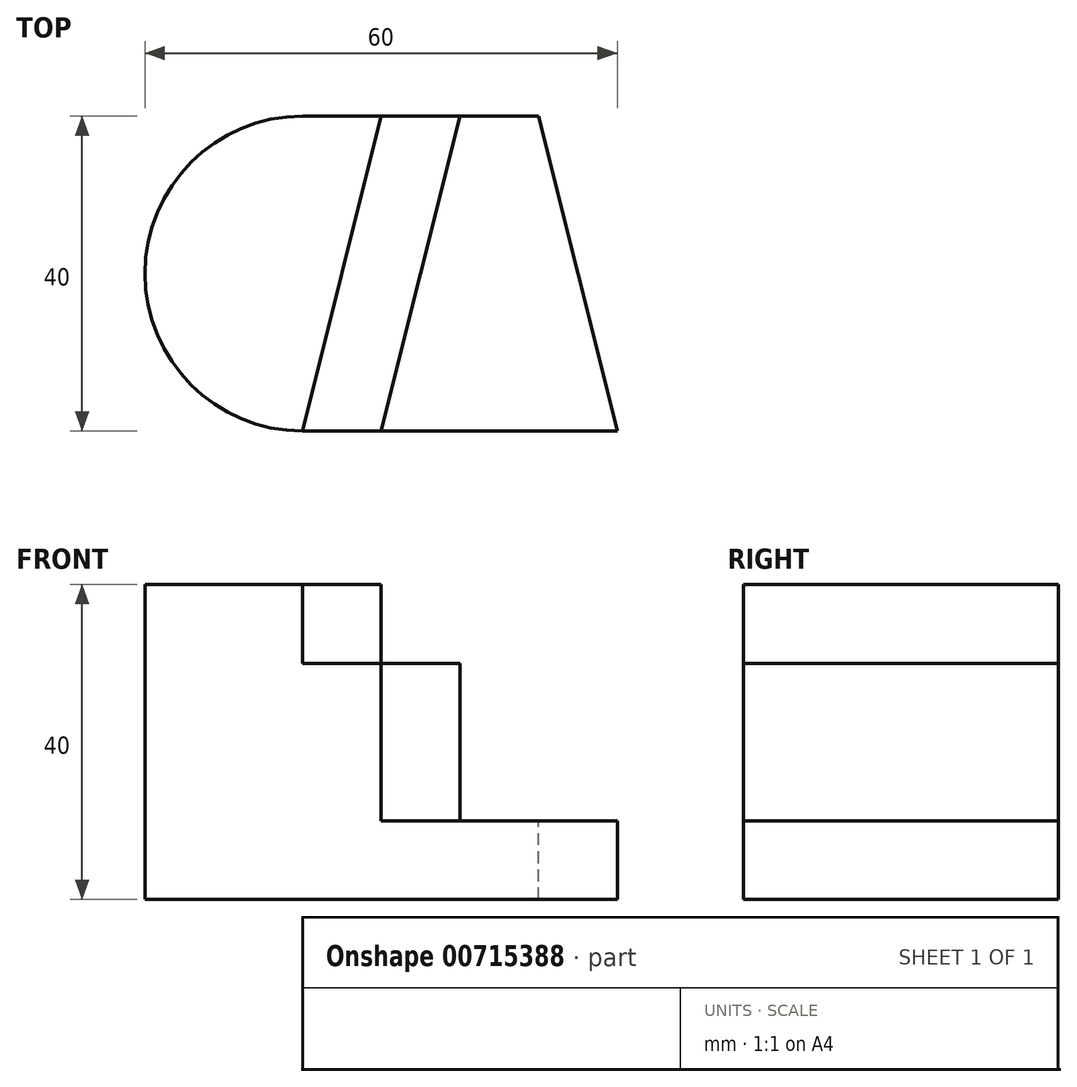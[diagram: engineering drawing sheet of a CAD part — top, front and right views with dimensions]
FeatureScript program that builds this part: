
annotation { "Feature Type Name" : "Feature", "Feature Type Description" : "" }
export const myFeature = defineFeature(function(context is Context, id is Id, definition is map)
    precondition{}
    {
        {
            var Q0;
            Q0=qCreatedBy(makeId("Top.planeOp"),FACE);
            var sketch = newSketch(context, id + "F0", { "sketchPlane" : qUnion([Q0])});
            skLineSegment(sketch, "E0.bottom", {"start": v(-26.07, 18.94) * mm, "end": v(33.93, 18.94) * mm});
            skLineSegment(sketch, "E0.top", {"start": v(-26.07, -21.06) * mm, "end": v(33.93, -21.06) * mm});
            skLineSegment(sketch, "E0.left", {"start": v(-26.07, 18.94) * mm, "end": v(-26.07, -21.06) * mm});
            skLineSegment(sketch, "E0.right", {"start": v(33.93, 18.94) * mm, "end": v(33.93, -21.06) * mm});
            skSolve(sketch);
        }
        {
            var Q0;
            Q0=makeQuery(id+"F0.imprint","IMPRINT",FACE,{"disambiguationData":[TD([[makeQuery(id+"F0.imprint","IMPRINT",EDGE,{"derivedFrom":sQuery(id+"F0.wireOp",EDGE,"E0.bottom")}),-1.0]])]});
            extrude(context, id + "F1", {"entities" : qUnion([Q0]), "depth" : 40 * mm, "offsetDistance" : 25.4 * mm});
        }
        {
            var Q0;
            Q0=makeQuery(id+"F1.opExtrude","SWEPT_EDGE",EDGE,{"disambiguationData":[OSD([sQuery(id+"F0.wireOp",EDGE,"E0.bottom"),sQuery(id+"F0.wireOp",EDGE,"E0.left")])]});
            var Q1;
            Q1=makeQuery(id+"F1.opExtrude","SWEPT_EDGE",EDGE,{"disambiguationData":[OSD([sQuery(id+"F0.wireOp",EDGE,"E0.top"),sQuery(id+"F0.wireOp",EDGE,"E0.left")])]});
            fillet(context, id + "F2", {"entities" : qUnion([Q0, Q1]), "radius" : 20 * mm, "tangentPropagation" : true, "allowEdgeOverflow" : false});
        }
        {
            var Q0;
            Q0=makeQuery(id+"F1.opExtrude","CAP_FACE",FACE,{"disambiguationData":[OSD([sQuery(id+"F0.wireOp",EDGE,"E0.bottom"),sQuery(id+"F0.wireOp",EDGE,"E0.top"),sQuery(id+"F0.wireOp",EDGE,"E0.left"),sQuery(id+"F0.wireOp",EDGE,"E0.right")])],"isStart":false});
            var sketch = newSketch(context, id + "F3", { "sketchPlane" : qUnion([Q0])});
            skLineSegment(sketch, "E1", {"start": v(33.93, 18.94) * mm, "end": v(23.93, 18.94) * mm});
            skLineSegment(sketch, "E2", {"start": v(23.93, 18.94) * mm, "end": v(33.93, -21.06) * mm});
            skSolve(sketch);
        }
        {
            var Q0;
            Q0=makeQuery(id+"F3.imprint","IMPRINT",FACE,{"disambiguationData":[TD([[makeQuery(id+"F3.imprint","IMPRINT",EDGE,{"derivedFrom":sQuery(id+"F3.wireOp",EDGE,"E1")}),-1.0]])]});
            extrude(context, id + "F4", {"entities" : qUnion([Q0]), "operationType" : NewBodyOperationType.REMOVE, "oppositeDirection" : true, "depth" : 40 * mm, "offsetDistance" : 25.4 * mm});
        }
        {
            var Q0;
            Q0=makeQuery(id+"F1.opExtrude","CAP_FACE",FACE,{"disambiguationData":[OSD([sQuery(id+"F0.wireOp",EDGE,"E0.bottom"),sQuery(id+"F0.wireOp",EDGE,"E0.top"),sQuery(id+"F0.wireOp",EDGE,"E0.left"),sQuery(id+"F0.wireOp",EDGE,"E0.right")])],"isStart":false});
            var sketch = newSketch(context, id + "F5", { "sketchPlane" : qUnion([Q0])});
            skLineSegment(sketch, "E3", {"start": v(23.93, 18.94) * mm, "end": v(13.93, 18.94) * mm});
            skLineSegment(sketch, "E4", {"start": v(13.93, 18.94) * mm, "end": v(3.93, -21.06) * mm});
            skLineSegment(sketch, "E5", {"start": v(3.93, -21.06) * mm, "end": v(33.93, -21.06) * mm});
            skLineSegment(sketch, "E6", {"start": v(33.93, -21.06) * mm, "end": v(23.93, 18.94) * mm});
            skSolve(sketch);
        }
        {
            var Q0;
            Q0=makeQuery(id+"F5.imprint","IMPRINT",FACE,{"disambiguationData":[TD([[makeQuery(id+"F5.imprint","IMPRINT",EDGE,{"derivedFrom":sQuery(id+"F5.wireOp",EDGE,"E3")}),-1.0]])]});
            extrude(context, id + "F6", {"entities" : qUnion([Q0]), "operationType" : NewBodyOperationType.REMOVE, "oppositeDirection" : true, "depth" : 30 * mm, "offsetDistance" : 25.4 * mm});
        }
        {
            var Q0;
            Q0=makeQuery(id+"F1.opExtrude","CAP_FACE",FACE,{"disambiguationData":[OSD([sQuery(id+"F0.wireOp",EDGE,"E0.bottom"),sQuery(id+"F0.wireOp",EDGE,"E0.top"),sQuery(id+"F0.wireOp",EDGE,"E0.left"),sQuery(id+"F0.wireOp",EDGE,"E0.right")])],"isStart":false});
            var sketch = newSketch(context, id + "F7", { "sketchPlane" : qUnion([Q0])});
            skLineSegment(sketch, "E7", {"start": v(13.93, 18.94) * mm, "end": v(3.93, 18.94) * mm});
            skLineSegment(sketch, "E8", {"start": v(3.93, 18.94) * mm, "end": v(-6.07, -21.06) * mm});
            skLineSegment(sketch, "E9", {"start": v(-6.07, -21.06) * mm, "end": v(3.93, -21.06) * mm});
            skLineSegment(sketch, "E10", {"start": v(3.93, -21.06) * mm, "end": v(13.93, 18.94) * mm});
            skSolve(sketch);
        }
        {
            var Q0;
            Q0=makeQuery(id+"F7.imprint","IMPRINT",FACE,{"disambiguationData":[TD([[makeQuery(id+"F7.imprint","IMPRINT",EDGE,{"derivedFrom":sQuery(id+"F7.wireOp",EDGE,"E7")}),-1.0]])]});
            extrude(context, id + "F8", {"entities" : qUnion([Q0]), "operationType" : NewBodyOperationType.REMOVE, "oppositeDirection" : true, "depth" : 10 * mm, "offsetDistance" : 25.4 * mm});
        }
    });
